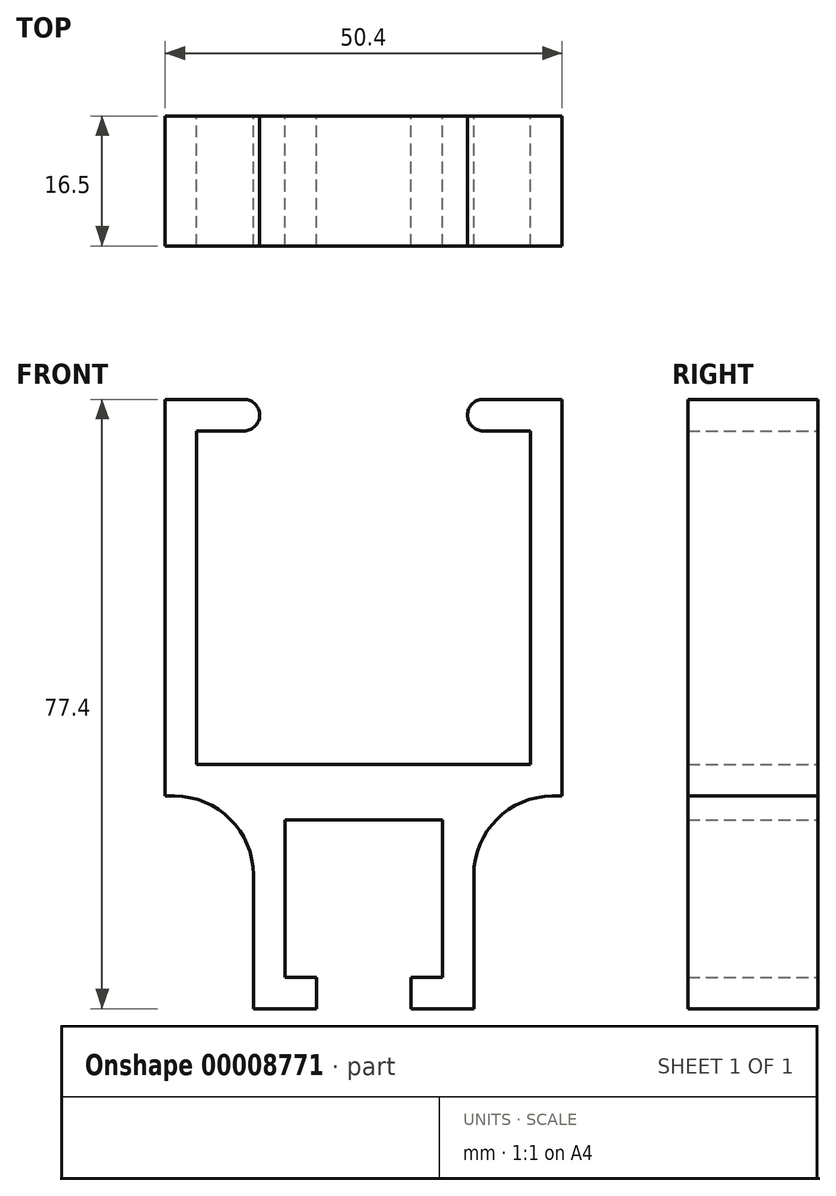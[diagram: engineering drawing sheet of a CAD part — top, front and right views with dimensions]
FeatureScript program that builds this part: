
annotation { "Feature Type Name" : "Feature", "Feature Type Description" : "" }
export const myFeature = defineFeature(function(context is Context, id is Id, definition is map)
    precondition{}
    {
        {
            var Q0;
            Q0=qCreatedBy(makeId("Front.planeOp"),FACE);
            var sketch = newSketch(context, id + "F0", { "sketchPlane" : qUnion([Q0])});
            skLineSegment(sketch, "E0", {"start": v(-10, -10) * mm, "end": v(-10, 10) * mm});
            skLineSegment(sketch, "E1", {"start": v(-10, 10) * mm, "end": v(10, 10) * mm});
            skLineSegment(sketch, "E2", {"start": v(10, 10) * mm, "end": v(10, -10) * mm});
            skLineSegment(sketch, "E3", {"start": v(10, -10) * mm, "end": v(6, -10) * mm});
            skLineSegment(sketch, "E4", {"start": v(6, -10) * mm, "end": v(6, -14) * mm});
            skLineSegment(sketch, "E5", {"start": v(6, -14) * mm, "end": v(14, -14) * mm});
            skLineSegment(sketch, "E6", {"start": v(14, -14) * mm, "end": v(14, 13) * mm});
            skLineSegment(sketch, "E7", {"start": v(-14, 13) * mm, "end": v(-14, -14) * mm});
            skLineSegment(sketch, "E8", {"start": v(-14, -14) * mm, "end": v(-6, -14) * mm});
            skLineSegment(sketch, "E9", {"start": v(-6, -14) * mm, "end": v(-6, -10) * mm});
            skLineSegment(sketch, "E10", {"start": v(-6, -10) * mm, "end": v(-10, -10) * mm});
            skLineSegment(sketch, "E11", {"start": v(0, 10) * mm, "end": v(0, -18.16) * mm, "construction": true});
            skLineSegment(sketch, "E12", {"start": v(-10, 10) * mm, "end": v(10, -10) * mm, "construction": true});
            skLineSegment(sketch, "E13", {"start": v(-10, -10) * mm, "end": v(10, 10) * mm, "construction": true});
            skLineSegment(sketch, "E14", {"start": v(14, 13) * mm, "end": v(25.2, 13) * mm});
            skLineSegment(sketch, "E15", {"start": v(25.2, 13) * mm, "end": v(25.2, 63.4) * mm});
            skLineSegment(sketch, "E16", {"start": v(25.2, 63.4) * mm, "end": v(13.2, 63.4) * mm});
            skLineSegment(sketch, "E17", {"start": v(13.2, 63.4) * mm, "end": v(13.2, 59.4) * mm});
            skLineSegment(sketch, "E18", {"start": v(13.2, 59.4) * mm, "end": v(21.2, 59.4) * mm});
            skLineSegment(sketch, "E19", {"start": v(21.2, 59.4) * mm, "end": v(21.2, 17) * mm});
            skLineSegment(sketch, "E20", {"start": v(21.2, 17) * mm, "end": v(0, 17) * mm});
            skLineSegment(sketch, "E21.0.MirrorCS", {"start": v(-13.2, 59.4) * mm, "end": v(-21.2, 59.4) * mm});
            skLineSegment(sketch, "E21.1.MirrorCS", {"start": v(-13.2, 63.4) * mm, "end": v(-13.2, 59.4) * mm});
            skLineSegment(sketch, "E21.2.MirrorCS", {"start": v(-25.2, 63.4) * mm, "end": v(-13.2, 63.4) * mm});
            skLineSegment(sketch, "E21.3.MirrorCS", {"start": v(-21.2, 59.4) * mm, "end": v(-21.2, 17) * mm});
            skLineSegment(sketch, "E21.4.MirrorCS", {"start": v(-21.2, 17) * mm, "end": v(0, 17) * mm});
            skLineSegment(sketch, "E21.5.MirrorCS", {"start": v(-25.2, 13) * mm, "end": v(-25.2, 63.4) * mm});
            skLineSegment(sketch, "E21.6.MirrorCS", {"start": v(-14, 13) * mm, "end": v(-25.2, 13) * mm});
            skPoint(sketch, "E22.orphan", {"position": v(0, 13) * mm});
            skSolve(sketch);
        }
        {
            var Q0;
            Q0 = qSketchRegion(id + "F0", true);
            extrude(context, id + "F1", {"entities" : qUnion([Q0]), "endBound" : BoundingType.SYMMETRIC, "depth" : 16.5 * mm});
        }
        {
            var Q0;
            Q0=makeQuery(id+"F1.opExtrude","SWEPT_EDGE",EDGE,{"disambiguationData":[OSD([sQuery(id+"F0.wireOp",EDGE,"E6"),sQuery(id+"F0.wireOp",EDGE,"E14")])]});
            var Q1;
            Q1=makeQuery(id+"F1.opExtrude","SWEPT_EDGE",EDGE,{"disambiguationData":[OSD([sQuery(id+"F0.wireOp",EDGE,"E7"),sQuery(id+"F0.wireOp",EDGE,"E21.6.MirrorCS")])]});
            fillet(context, id + "F2", {"entities" : qUnion([Q0, Q1]), "radius" : 10 * mm, "tangentPropagation" : true, "allowEdgeOverflow" : false});
        }
        {
            var Q0;
            Q0=makeQuery(id+"F1.opExtrude","SWEPT_EDGE",EDGE,{"disambiguationData":[OSD([sQuery(id+"F0.wireOp",EDGE,"E21.0.MirrorCS"),sQuery(id+"F0.wireOp",EDGE,"E21.1.MirrorCS")])]});
            var Q1;
            Q1=makeQuery(id+"F1.opExtrude","SWEPT_EDGE",EDGE,{"disambiguationData":[OSD([sQuery(id+"F0.wireOp",EDGE,"E21.1.MirrorCS"),sQuery(id+"F0.wireOp",EDGE,"E21.2.MirrorCS")])]});
            var Q2;
            Q2=makeQuery(id+"F1.opExtrude","SWEPT_EDGE",EDGE,{"disambiguationData":[OSD([sQuery(id+"F0.wireOp",EDGE,"E16"),sQuery(id+"F0.wireOp",EDGE,"E17")])]});
            var Q3;
            Q3=makeQuery(id+"F1.opExtrude","SWEPT_EDGE",EDGE,{"disambiguationData":[OSD([sQuery(id+"F0.wireOp",EDGE,"E17"),sQuery(id+"F0.wireOp",EDGE,"E18")])]});
            fillet(context, id + "F3", {"entities" : qUnion([Q0, Q1, Q2, Q3]), "radius" : 2 * mm, "tangentPropagation" : true, "allowEdgeOverflow" : false});
        }
    });
